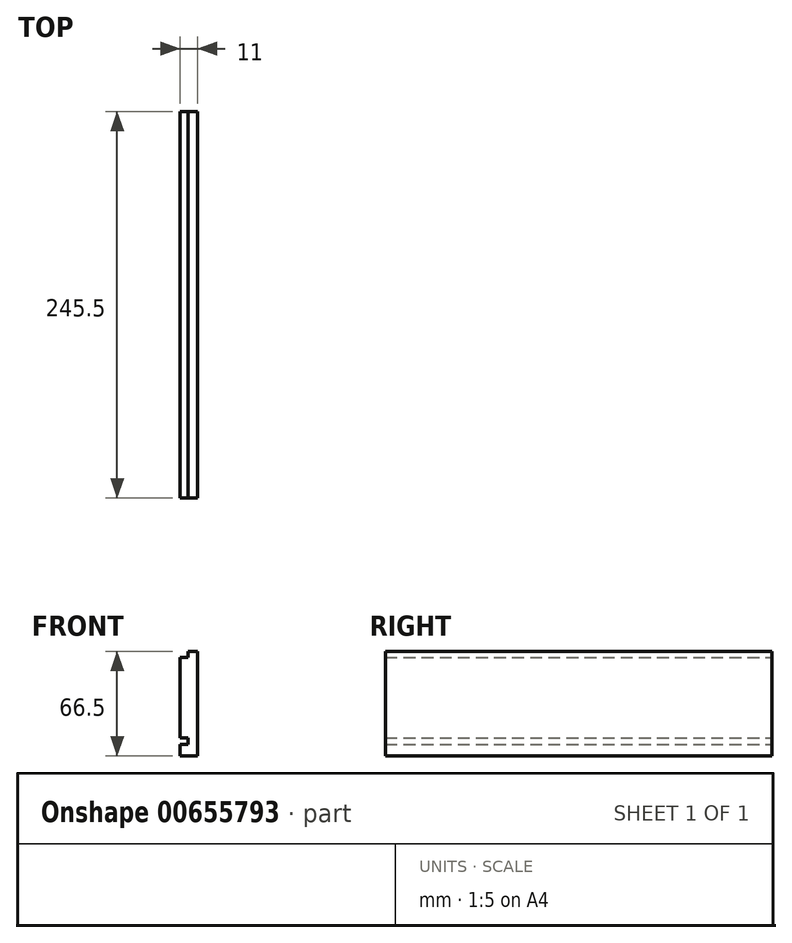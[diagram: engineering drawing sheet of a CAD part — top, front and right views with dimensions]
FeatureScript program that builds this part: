
annotation { "Feature Type Name" : "Feature", "Feature Type Description" : "" }
export const myFeature = defineFeature(function(context is Context, id is Id, definition is map)
    precondition{}
    {
        {
            var Q0;
            Q0=qCreatedBy(makeId("Front.planeOp"),FACE);
            var sketch = newSketch(context, id + "F0", { "sketchPlane" : qUnion([Q0])});
            skLineSegment(sketch, "E0", {"start": v(0, -2.5) * mm, "end": v(0, 66.5) * mm});
            skLineSegment(sketch, "E1", {"start": v(0, 66.5) * mm, "end": v(-6, 66.5) * mm});
            skLineSegment(sketch, "E2", {"start": v(-6, 62.55) * mm, "end": v(-11, 62.55) * mm});
            skLineSegment(sketch, "E3", {"start": v(-11, 62.55) * mm, "end": v(-6, 62.55) * mm});
            skLineSegment(sketch, "E4", {"start": v(-6, 66.5) * mm, "end": v(-6, 62.55) * mm});
            skLineSegment(sketch, "E5", {"start": v(-11, 62.55) * mm, "end": v(-11, 11.55) * mm});
            skLineSegment(sketch, "E6", {"start": v(-11, 11.55) * mm, "end": v(-6, 11.55) * mm});
            skLineSegment(sketch, "E7", {"start": v(-6, 11.55) * mm, "end": v(-6, 7.55) * mm});
            skLineSegment(sketch, "E8", {"start": v(-6, 7.55) * mm, "end": v(-11, 7.55) * mm});
            skLineSegment(sketch, "E9", {"start": v(-11, 7.55) * mm, "end": v(-11, 0) * mm});
            skLineSegment(sketch, "E10", {"start": v(-11, 0) * mm, "end": v(0, 0) * mm});
            skSolve(sketch);
        }
        {
            var Q0;
            {var subQ0=sQuery(id+"F0.wireOp",EDGE,"E1");Q0=makeQuery(id+"F0.imprint","IMPRINT",FACE,{"disambiguationData":[TD([[makeQuery(id+"F0.imprint","IMPRINT",EDGE,{"derivedFrom":subQ0}),1.0]])]});}
            extrude(context, id + "F1", {"entities" : qUnion([Q0]), "depth" : 245.5 * mm, "offsetDistance" : 25 * mm});
        }
    });
